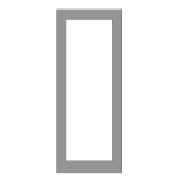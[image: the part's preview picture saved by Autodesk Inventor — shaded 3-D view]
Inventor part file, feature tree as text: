
AUTODESK INVENTOR PART (.ipt)
format: ipt  version: 2020 (Build 240168000, 168)  size: 130,560 bytes
history: native  units: in
note: dims shown in document units (in); Inventor stores cm internally (conversion verified against a paired STEP export)
features: other x4, plane x3, sketch x3, split x2
ambient origin geometry x8: Origin, YZ Plane, XZ Plane, XY Plane, X Axis, Y Axis, Z Axis, Center Point
bodies: Solid1 (feature_tree), Body (feature_tree)
feature tree (12):
  other  "Driven Length"
  other  "Frame Generator"
  other  "Start Plane"
  other  "End Plane"
  plane  "Work Plane6"
  split  "Split1"
  plane  "Work Plane7"
  split  "Split2"
  sketch  "Sketch"  dims[d2=0.125in d3=0.125in d6=0.5in d7=23.5in d8=0.13in d9=0.0in d14=90.0deg d11=23.0in]
  sketch  "Sketch6"  dims[d0=1.0in]
  plane  "Work Plane5"
  sketch  "Sketch7"  dims[d1=3.0in]
